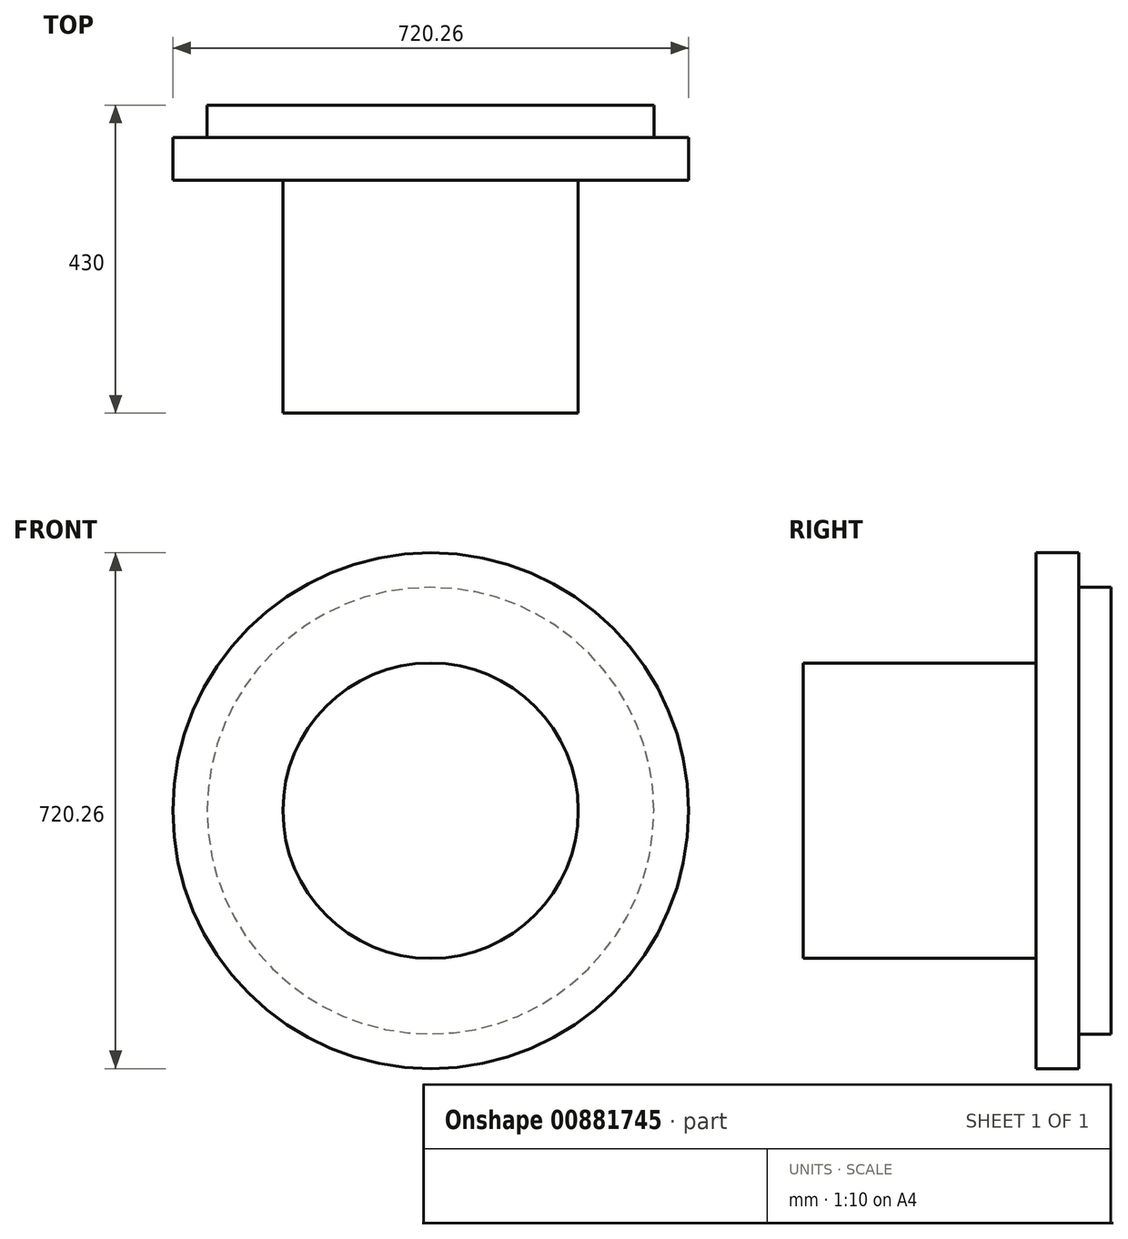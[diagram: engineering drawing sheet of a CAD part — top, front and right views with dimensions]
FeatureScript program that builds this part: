
annotation { "Feature Type Name" : "Feature", "Feature Type Description" : "" }
export const myFeature = defineFeature(function(context is Context, id is Id, definition is map)
    precondition{}
    {
        {
            var Q0;
            Q0=qCreatedBy(makeId("Front.planeOp"),FACE);
            var sketch = newSketch(context, id + "F0", { "sketchPlane" : qUnion([Q0])});
            skCircle(sketch, "E0", {"center": v(0, 0) * mm, "radius": 0.15 * mm});
            skCircle(sketch, "E1", {"center": v(0.15, 0) * mm, "radius": 0.15 * mm});
            skCircle(sketch, "E2", {"center": v(0.3, 0) * mm, "radius": 0.15 * mm});
            skCircle(sketch, "E3", {"center": v(0.45, 0) * mm, "radius": 0.15 * mm});
            skSolve(sketch);
        }
        {
            var Q0;
            Q0=qCreatedBy(makeId("Right.planeOp"),FACE);
            cPlane(context, id + "F1", {"entities" : qUnion([Q0]), "cplaneType" : CPlaneType.OFFSET, "offset" : 0.15 * mm, "width" : 150 * mm, "height" : 150 * mm});
        }
        {
            var Q0;
            Q0=qCreatedBy(id+"F1.planeOp",FACE);
            cPlane(context, id + "F2", {"entities" : qUnion([Q0]), "cplaneType" : CPlaneType.OFFSET, "offset" : .15 * mm, "width" : 150 * mm, "height" : 150 * mm});
        }
        {
            var Q0;
            Q0=qCreatedBy(makeId("Front.planeOp"),FACE);
            var sketch = newSketch(context, id + "F3", { "sketchPlane" : qUnion([Q0])});
            skCircle(sketch, "E4", {"center": v(0.15, 0) * mm, "radius": 311.83 * mm});
            skSolve(sketch);
        }
        {
            var Q0;
            Q0=makeQuery(id+"F3.imprint","IMPRINT",FACE,{"disambiguationData":[TD([[makeQuery(id+"F3.imprint","IMPRINT",EDGE,{"derivedFrom":sQuery(id+"F3.wireOp",EDGE,"E4")}),1.0]])]});
            extrude(context, id + "F4", {"entities" : qUnion([Q0]), "oppositeDirection" : true, "depth" : 45 * mm, "offsetDistance" : 25 * mm});
        }
        {
            var Q0;
            Q0=makeQuery(id+"F4.opExtrude","CAP_FACE",FACE,{"disambiguationData":[OSD([sQuery(id+"F3.wireOp",EDGE,"E4")])],"isStart":true});
            var sketch = newSketch(context, id + "F5", { "sketchPlane" : qUnion([Q0])});
            skCircle(sketch, "E5", {"center": v(0.3, 0) * mm, "radius": 206.25 * mm});
            skSolve(sketch);
        }
        {
            var Q0;
            Q0 = qSketchRegion(id + "F5", true);
            extrude(context, id + "F6", {"entities" : qUnion([Q0]), "operationType" : NewBodyOperationType.ADD, "depth" : 385 * mm, "offsetDistance" : 25 * mm});
        }
        {
            var Q0;
            Q0=makeQuery(id+"F4.opExtrude","CAP_FACE",FACE,{"disambiguationData":[OSD([sQuery(id+"F3.wireOp",EDGE,"E4")])],"isStart":true});
            var sketch = newSketch(context, id + "F7", { "sketchPlane" : qUnion([Q0])});
            skCircle(sketch, "E6", {"center": v(0.45, 0) * mm, "radius": 360.12 * mm});
            skSolve(sketch);
        }
        {
            var Q0;
            Q0 = qSketchRegion(id + "F7", true);
            extrude(context, id + "F8", {"entities" : qUnion([Q0]), "operationType" : NewBodyOperationType.ADD, "depth" : 60 * mm, "offsetDistance" : 25 * mm});
        }
    });
